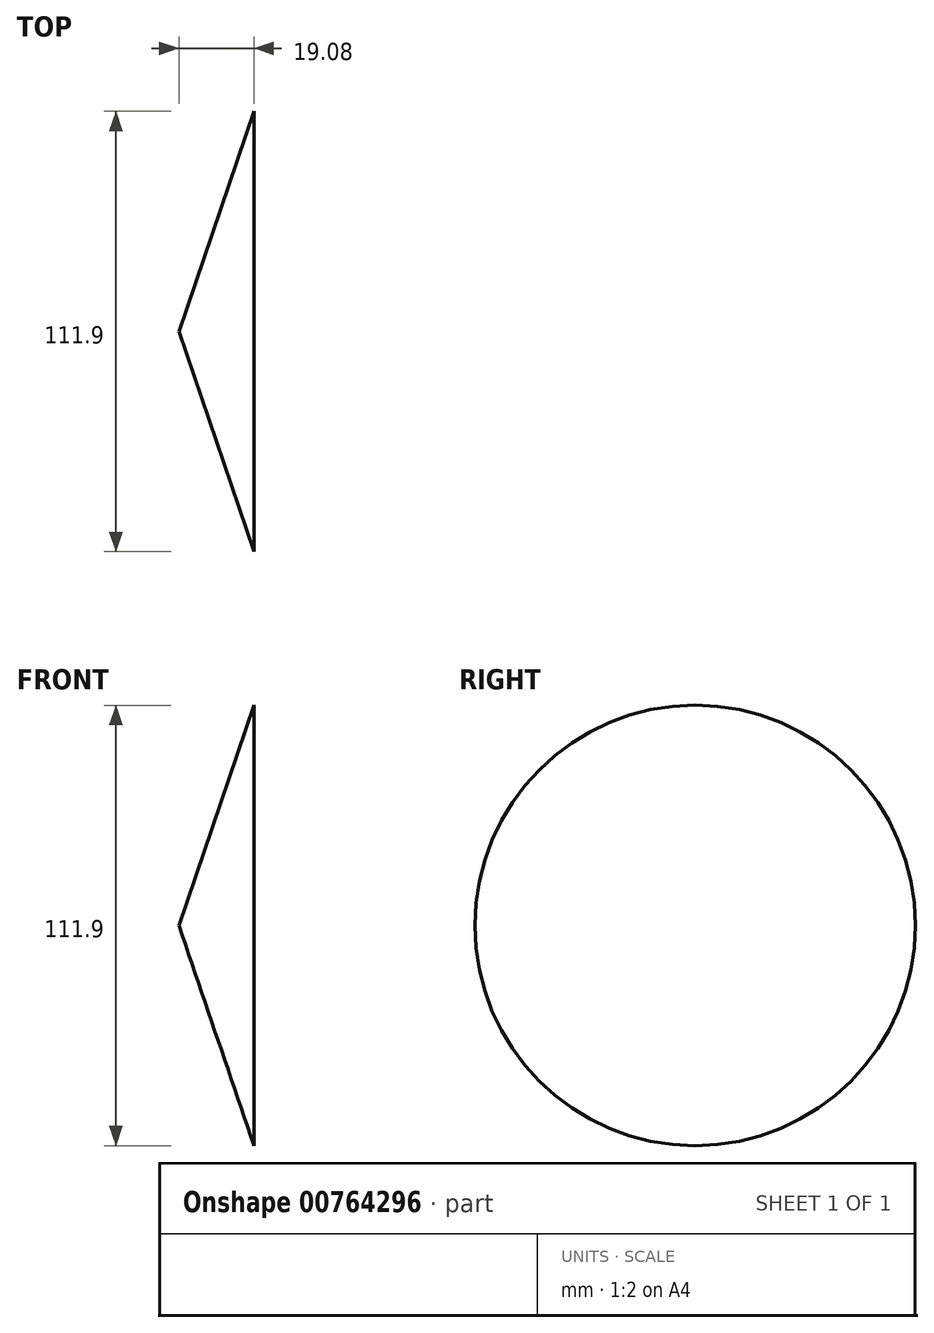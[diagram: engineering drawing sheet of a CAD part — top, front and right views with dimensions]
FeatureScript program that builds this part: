
annotation { "Feature Type Name" : "Feature", "Feature Type Description" : "" }
export const myFeature = defineFeature(function(context is Context, id is Id, definition is map)
    precondition{}
    {
        {
            var Q0;
            Q0=qCreatedBy(makeId("Front.planeOp"),FACE);
            var sketch = newSketch(context, id + "F0", { "sketchPlane" : qUnion([Q0])});
            skLineSegment(sketch, "E0", {"start": v(0, 55.95) * mm, "end": v(-19.08, 0) * mm});
            skLineSegment(sketch, "E1", {"start": v(-19.08, 0) * mm, "end": v(0, 0) * mm});
            skLineSegment(sketch, "E2", {"start": v(0, 0) * mm, "end": v(0, 55.95) * mm});
            skSolve(sketch);
        }
        {
            var Q0;
            Q0 = qSketchRegion(id + "F0", true);
            var Q1;
            Q1=sQuery(id+"F0.wireOp",EDGE,"E1");
            revolve(context, id + "F1", {"surfaceOperationType" : NewSurfaceOperationType.NEW, "entities" : qUnion([Q0]), "axis" : qUnion([Q1]), "revolveType" : RevolveType.FULL});
        }
    });
